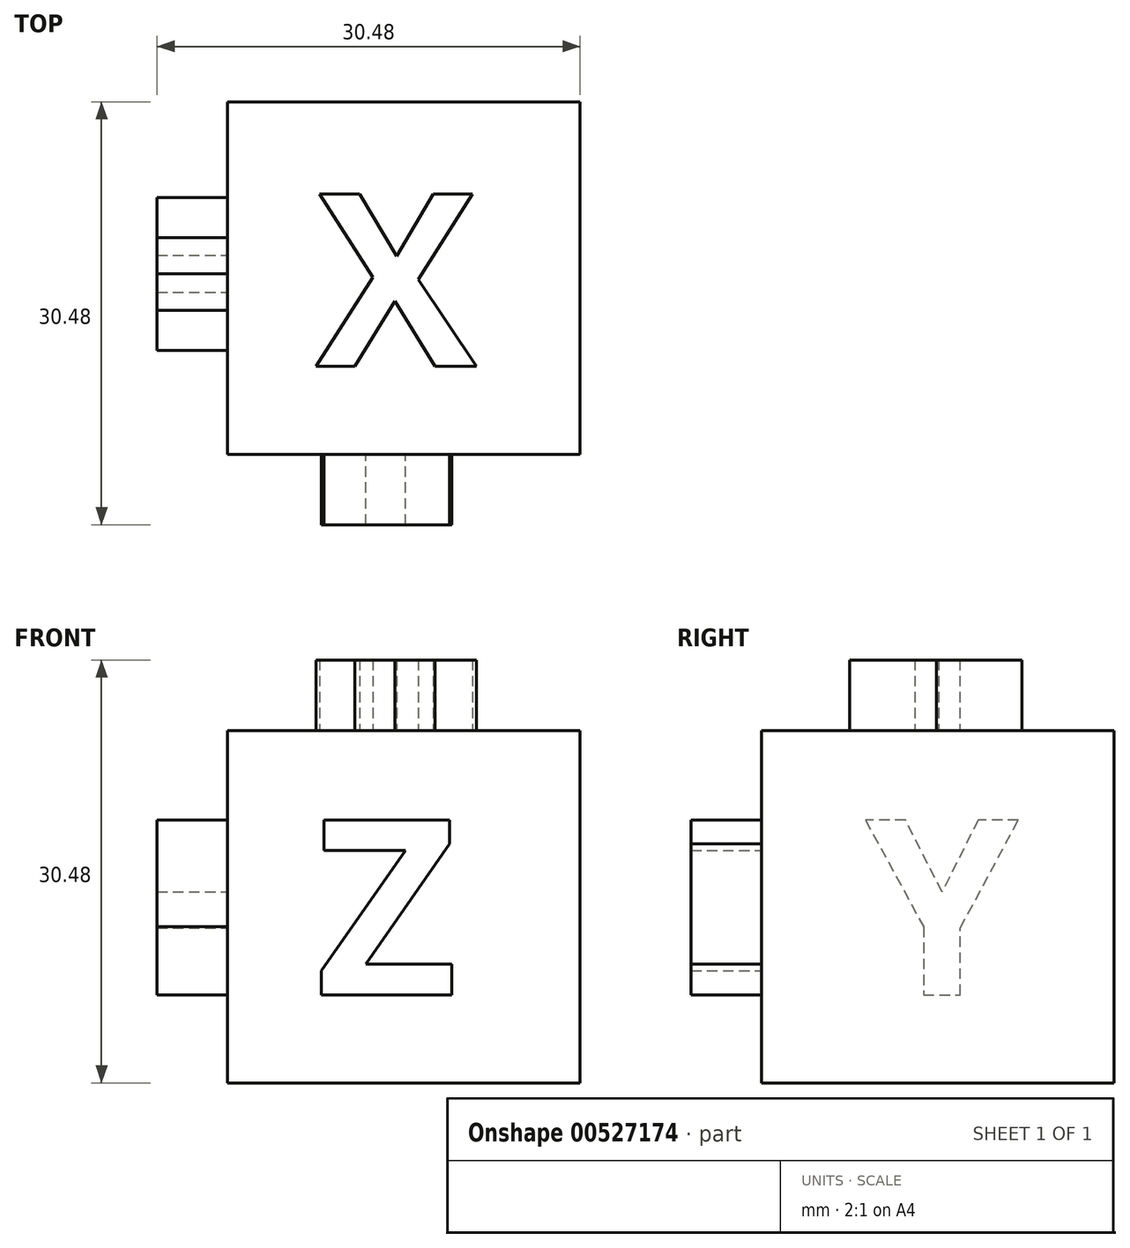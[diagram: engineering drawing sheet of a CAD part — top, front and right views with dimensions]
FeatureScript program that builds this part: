
annotation { "Feature Type Name" : "Feature", "Feature Type Description" : "" }
export const myFeature = defineFeature(function(context is Context, id is Id, definition is map)
    precondition{}
    {
        {
            var Q0;
            Q0=qCreatedBy(makeId("Front.planeOp"),FACE);
            var sketch = newSketch(context, id + "F0", { "sketchPlane" : qUnion([Q0])});
            skLineSegment(sketch, "E0.bottom", {"start": v(-12.7, 12.7) * mm, "end": v(12.7, 12.7) * mm});
            skLineSegment(sketch, "E0.top", {"start": v(-12.7, -12.7) * mm, "end": v(12.7, -12.7) * mm});
            skLineSegment(sketch, "E0.left", {"start": v(-12.7, 12.7) * mm, "end": v(-12.7, -12.7) * mm});
            skLineSegment(sketch, "E0.right", {"start": v(12.7, 12.7) * mm, "end": v(12.7, -12.7) * mm});
            skSolve(sketch);
        }
        {
            var Q0;
            Q0=qSketchRegion(id+"F0",true);
            extrude(context, id + "F1", {"entities" : qUnion([Q0]), "endBound" : BoundingType.SYMMETRIC, "depth" : 25.4 * mm});
        }
        {
            var Q0;
            Q0=makeQuery(id+"F1.opExtrude","CAP_FACE",FACE,{"disambiguationData":[OSD([sQuery(id+"F0.wireOp",EDGE,"E0.bottom"),sQuery(id+"F0.wireOp",EDGE,"E0.top"),sQuery(id+"F0.wireOp",EDGE,"E0.left"),sQuery(id+"F0.wireOp",EDGE,"E0.right")])],"isStart":false});
            var sketch = newSketch(context, id + "F2", { "sketchPlane" : qUnion([Q0])});
            skText(sketch, "E1", { "text": "Z", "fontName": "OpenSans-Bold.ttf"});
            const initialGuessF2  = {"E1": [-0.00635, -0.00635, 1, 0, 0.0127]};
            skSetInitialGuess(sketch, initialGuessF2);
            skSolve(sketch);
        }
        {
            var Q0;
            Q0=qSketchRegion(id+"F2",true);
            extrude(context, id + "F3", {"entities" : qUnion([Q0]), "depth" : 5.08 * mm});
        }
        {
            var Q0;
            Q0=makeQuery(id+"F1.opExtrude","SWEPT_FACE",FACE,{"disambiguationData":[OSD([sQuery(id+"F0.wireOp",EDGE,"E0.bottom")])]});
            var sketch = newSketch(context, id + "F4", { "sketchPlane" : qUnion([Q0])});
            skText(sketch, "E2", { "text": "X", "fontName": "OpenSans-Bold.ttf"});
            const initialGuessF4  = {"E2": [-0.00634, -0.00635, 1, 0, 0.0125]};
            skSetInitialGuess(sketch, initialGuessF4);
            skSolve(sketch);
        }
        {
            var Q0;
            Q0=qSketchRegion(id+"F4",true);
            extrude(context, id + "F5", {"entities" : qUnion([Q0]), "depth" : 5.08 * mm});
        }
        {
            var Q0;
            Q0=makeQuery(id+"F1.opExtrude","SWEPT_FACE",FACE,{"disambiguationData":[OSD([sQuery(id+"F0.wireOp",EDGE,"E0.left")])]});
            var sketch = newSketch(context, id + "F6", { "sketchPlane" : qUnion([Q0])});
            skText(sketch, "E3", { "text": "Y", "fontName": "OpenSans-Bold.ttf"});
            const initialGuessF6  = {"E3": [-0.0058, -0.00635, 1, 0, 0.0127]};
            skSetInitialGuess(sketch, initialGuessF6);
            skSolve(sketch);
        }
        {
            var Q0;
            Q0=qSketchRegion(id+"F6",true);
            extrude(context, id + "F7", {"entities" : qUnion([Q0]), "depth" : 5.08 * mm});
        }
    });
